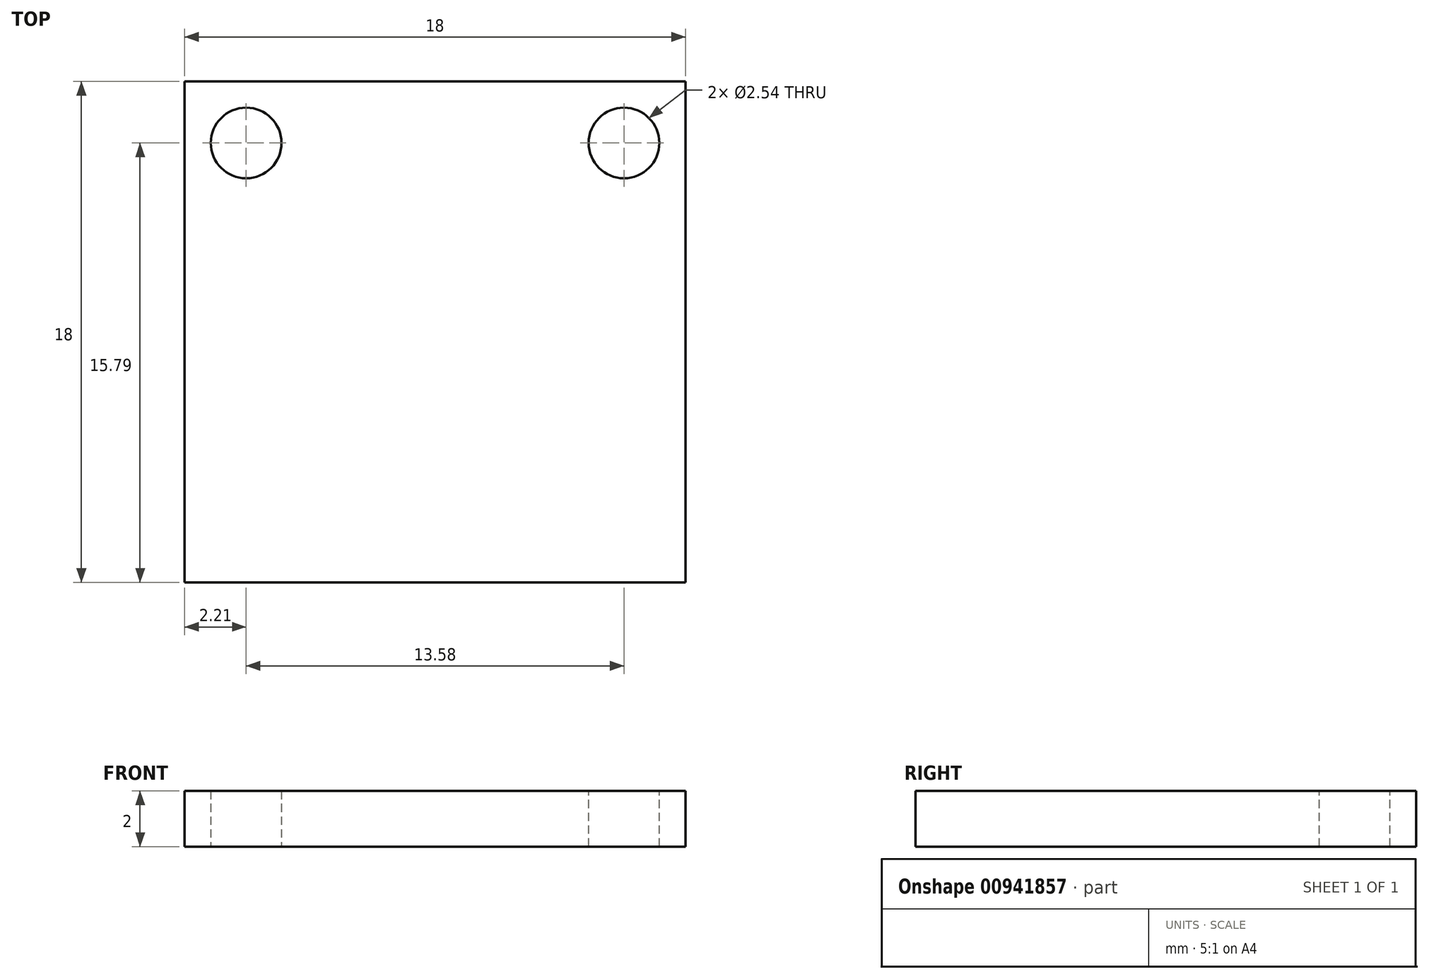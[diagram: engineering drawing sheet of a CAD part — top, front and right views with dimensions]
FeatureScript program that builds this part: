
annotation { "Feature Type Name" : "Feature", "Feature Type Description" : "" }
export const myFeature = defineFeature(function(context is Context, id is Id, definition is map)
    precondition{}
    {
        {
            var Q0;
            Q0=qCreatedBy(makeId("Top.planeOp"),FACE);
            var sketch = newSketch(context, id + "F0", { "sketchPlane" : qUnion([Q0])});
            skLineSegment(sketch, "E0.bottom", {"start": v(-9, 9) * mm, "end": v(9, 9) * mm});
            skLineSegment(sketch, "E0.top", {"start": v(-9, -9) * mm, "end": v(9, -9) * mm});
            skLineSegment(sketch, "E0.left", {"start": v(-9, 9) * mm, "end": v(-9, -9) * mm});
            skLineSegment(sketch, "E0.right", {"start": v(9, 9) * mm, "end": v(9, -9) * mm});
            skPoint(sketch, "E0.middle", {"position": v(0, 0) * mm});
            skSolve(sketch);
        }
        {
            var Q0;
            Q0=makeQuery(id+"F0.imprint","IMPRINT",FACE,{"disambiguationData":[TD([[makeQuery(id+"F0.imprint","IMPRINT",EDGE,{"derivedFrom":sQuery(id+"F0.wireOp",EDGE,"E0.bottom")}),-1.0]])]});
            extrude(context, id + "F1", {"entities" : qUnion([Q0]), "depth" : 2 * mm, "offsetDistance" : 25.4 * mm});
        }
        {
            var Q0;
            Q0=makeQuery(id+"F1.opExtrude","CAP_FACE",FACE,{"disambiguationData":[OSD([sQuery(id+"F0.wireOp",EDGE,"E0.bottom"),sQuery(id+"F0.wireOp",EDGE,"E0.top"),sQuery(id+"F0.wireOp",EDGE,"E0.left"),sQuery(id+"F0.wireOp",EDGE,"E0.right")])],"isStart":false});
            var sketch = newSketch(context, id + "F2", { "sketchPlane" : qUnion([Q0])});
            skCircle(sketch, "E1", {"center": v(6.8, 6.8) * mm, "radius": 1.66 * mm});
            skSolve(sketch);
        }
        {
            var Q0;
            Q0=sQuery(id+"F2.wireOp",VERTEX,"E1.center");
            var Q1;
            Q1=makeQuery(id+"F1.opExtrude","SWEPT_BODY",BODY,{"disambiguationData":[OSD([sQuery(id+"F0.wireOp",EDGE,"E0.bottom"),sQuery(id+"F0.wireOp",EDGE,"E0.top"),sQuery(id+"F0.wireOp",EDGE,"E0.left"),sQuery(id+"F0.wireOp",EDGE,"E0.right")])]});
            hole(context, id + "F3", {"style" : HoleStyle.SIMPLE, "endStyle" : HoleEndStyle.THROUGH, "holeDiameter" : 2.54 * mm, "majorDiameter" : 6.35 * mm, "isTappedThrough" : true, "tappedDepth" : 12.7 * mm, "tapClearance" : 3, "locations" : qUnion([Q0]), "scope" : qUnion([Q1])});
        }
        {
            var Q0;
            Q0=qCreatedBy(makeId("Top.planeOp"),FACE);
            var sketch = newSketch(context, id + "F4", { "sketchPlane" : qUnion([Q0])});
            skCircle(sketch, "E2", {"center": v(-6.8, 6.8) * mm, "radius": 1.52 * mm});
            skSolve(sketch);
        }
        {
            var Q0;
            Q0=sQuery(id+"F4.wireOp",VERTEX,"E2.center");
            var Q1;
            Q1=makeQuery(id+"F1.opExtrude","SWEPT_BODY",BODY,{"disambiguationData":[OSD([sQuery(id+"F0.wireOp",EDGE,"E0.bottom"),sQuery(id+"F0.wireOp",EDGE,"E0.top"),sQuery(id+"F0.wireOp",EDGE,"E0.left"),sQuery(id+"F0.wireOp",EDGE,"E0.right")])]});
            hole(context, id + "F5", {"style" : HoleStyle.SIMPLE, "endStyle" : HoleEndStyle.THROUGH, "oppositeDirection" : true, "holeDiameter" : 2.54 * mm, "majorDiameter" : 6.35 * mm, "isTappedThrough" : true, "tappedDepth" : 12.7 * mm, "tapClearance" : 3, "locations" : qUnion([Q0]), "scope" : qUnion([Q1])});
        }
    });
